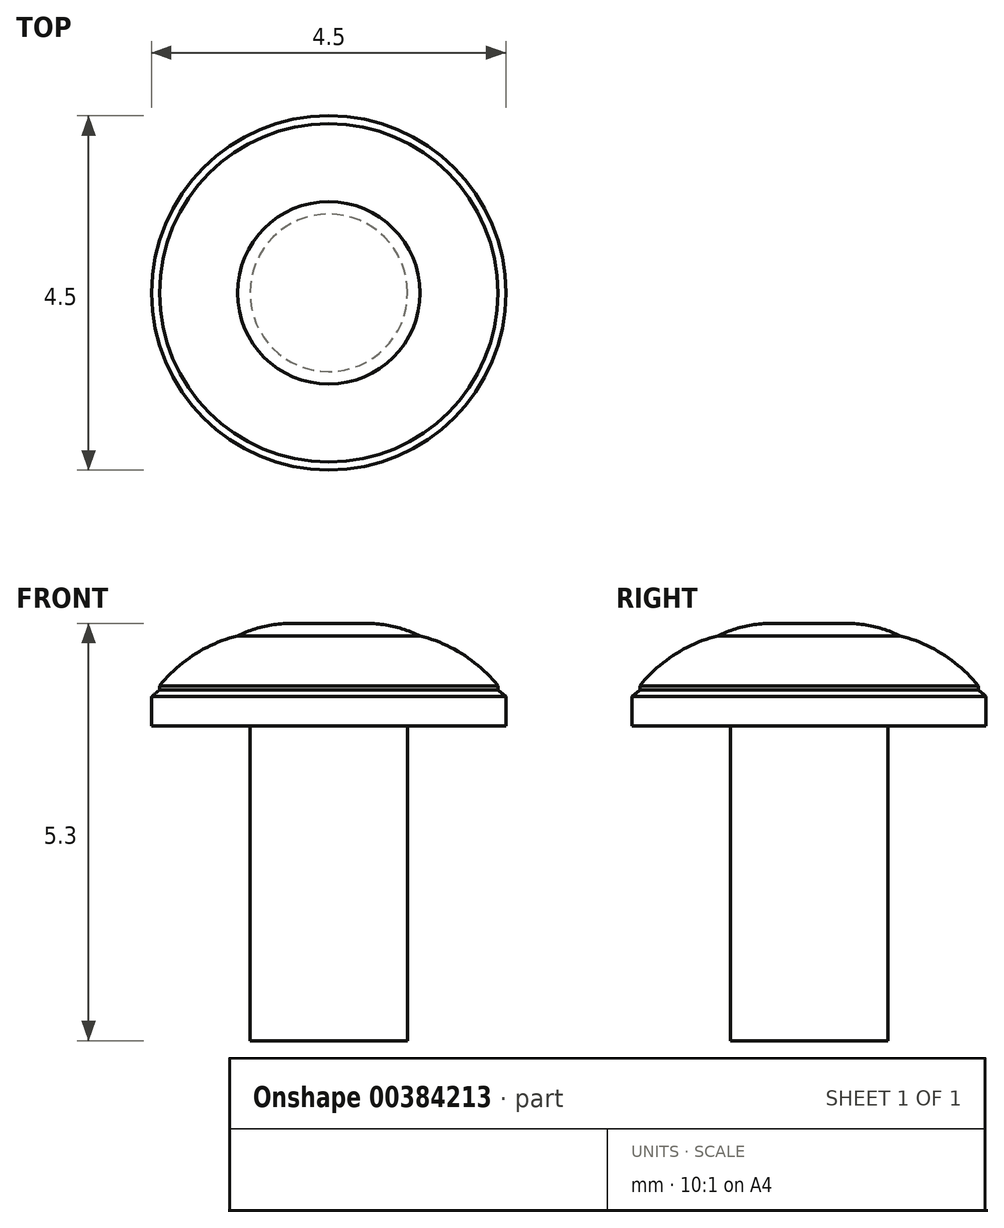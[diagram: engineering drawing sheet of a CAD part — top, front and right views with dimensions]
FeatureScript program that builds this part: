
annotation { "Feature Type Name" : "Feature", "Feature Type Description" : "" }
export const myFeature = defineFeature(function(context is Context, id is Id, definition is map)
    precondition{}
    {
        {
            var Q0;
            Q0=qCreatedBy(makeId("Front.planeOp"),FACE);
            var sketch = newSketch(context, id + "F0", { "sketchPlane" : qUnion([Q0])});
            skLineSegment(sketch, "E0", {"start": v(0, 0) * mm, "end": v(1.75, 0) * mm});
            skLineSegment(sketch, "E1", {"start": v(1.75, 0) * mm, "end": v(1.75, 0.63) * mm});
            skLineSegment(sketch, "E2", {"start": v(0, 1.3) * mm, "end": v(0.49, 1.3) * mm});
            skArc(sketch, "E3", {"start": v(1.75, 0.63) * mm, "mid": v(1.2, 1.12) * mm, "end": v(0.49, 1.3) * mm});
            skLineSegment(sketch, "E4", {"start": v(0, 1.3) * mm, "end": v(0, 0) * mm});
            skSolve(sketch);
        }
        {
            var Q0;
            Q0 = qSketchRegion(id + "F0", true);
            var Q1;
            Q1=sQuery(id+"F0.wireOp",EDGE,"E4");
            revolve(context, id + "F1", {"entities" : qUnion([Q0]), "axis" : qUnion([Q1]), "revolveType" : RevolveType.FULL});
        }
        {
            var Q0;
            Q0=makeQuery(id+"F1.opRevolve","SWEPT_FACE",FACE,{"disambiguationData":[OSD([sQuery(id+"F0.wireOp",EDGE,"E0")])]});
            var sketch = newSketch(context, id + "F2", { "sketchPlane" : qUnion([Q0])});
            skCircle(sketch, "E5", {"center": v(0, 0) * mm, "radius": 1 * mm});
            skSolve(sketch);
        }
        {
            var Q0;
            Q0 = qSketchRegion(id + "F2", true);
            extrude(context, id + "F3", {"entities" : qUnion([Q0]), "operationType" : NewBodyOperationType.ADD, "depth" : 4 * mm});
        }
        {
            var Q0;
            Q0=qCreatedBy(makeId("Front.planeOp"),FACE);
            var sketch = newSketch(context, id + "F4", { "sketchPlane" : qUnion([Q0])});
            skLineSegment(sketch, "E6", {"start": v(0, 0) * mm, "end": v(-2.15, 0) * mm});
            skLineSegment(sketch, "E7", {"start": v(-2.15, 0) * mm, "end": v(-2.15, 0.5) * mm});
            skLineSegment(sketch, "E8", {"start": v(0, 0) * mm, "end": v(0, 1.2) * mm});
            skLineSegment(sketch, "E9", {"start": v(0, 1.2) * mm, "end": v(-0.7, 1.2) * mm});
            skArc(sketch, "E10", {"start": v(-0.7, 1.2) * mm, "mid": v(-1.5, 1.02) * mm, "end": v(-2.15, 0.5) * mm});
            skSolve(sketch);
        }
        {
            var Q0;
            Q0 = qSketchRegion(id + "F4", true);
            var Q1;
            Q1=sQuery(id+"F4.wireOp",EDGE,"E8");
            revolve(context, id + "F5", {"entities" : qUnion([Q0]), "axis" : qUnion([Q1]), "revolveType" : RevolveType.FULL});
        }
        {
            var Q0;
            Q0=makeQuery(id+"F5.opRevolve","SWEPT_FACE",FACE,{"disambiguationData":[OSD([sQuery(id+"F4.wireOp",EDGE,"E6")])]});
            var sketch = newSketch(context, id + "F6", { "sketchPlane" : qUnion([Q0])});
            skCircle(sketch, "E11", {"center": v(0, 0) * mm, "radius": 1 * mm});
            skSolve(sketch);
        }
        {
            var Q0;
            Q0 = qSketchRegion(id + "F6", true);
            extrude(context, id + "F7", {"entities" : qUnion([Q0]), "operationType" : NewBodyOperationType.ADD, "depth" : 4 * mm});
        }
        {
            var Q0;
            Q0=qCreatedBy(makeId("Front.planeOp"),FACE);
            var sketch = newSketch(context, id + "F8", { "sketchPlane" : qUnion([Q0])});
            skArc(sketch, "E12", {"start": v(2.25, 0.37) * mm, "mid": v(1.2, 0.99) * mm, "end": v(0, 1.2) * mm});
            skLineSegment(sketch, "E13", {"start": v(2.25, 0.37) * mm, "end": v(2.25, 0) * mm});
            skLineSegment(sketch, "E14", {"start": v(2.25, 0) * mm, "end": v(0, 0) * mm});
            skLineSegment(sketch, "E15", {"start": v(0, 0) * mm, "end": v(0, 1.2) * mm});
            skSolve(sketch);
        }
        {
            var Q0;
            Q0 = qSketchRegion(id + "F8", true);
            var Q1;
            Q1=sQuery(id+"F8.wireOp",EDGE,"E15");
            revolve(context, id + "F9", {"entities" : qUnion([Q0]), "axis" : qUnion([Q1]), "revolveType" : RevolveType.FULL});
        }
        {
            var Q0;
            Q0=makeQuery(id+"F9.opRevolve","SWEPT_FACE",FACE,{"disambiguationData":[OSD([sQuery(id+"F8.wireOp",EDGE,"E14")])]});
            var sketch = newSketch(context, id + "F10", { "sketchPlane" : qUnion([Q0])});
            skCircle(sketch, "E16", {"center": v(0, 0) * mm, "radius": 1 * mm});
            skSolve(sketch);
        }
        {
            var Q0;
            Q0 = qSketchRegion(id + "F10", true);
            extrude(context, id + "F11", {"entities" : qUnion([Q0]), "operationType" : NewBodyOperationType.ADD, "depth" : 4 * mm});
        }
    });
